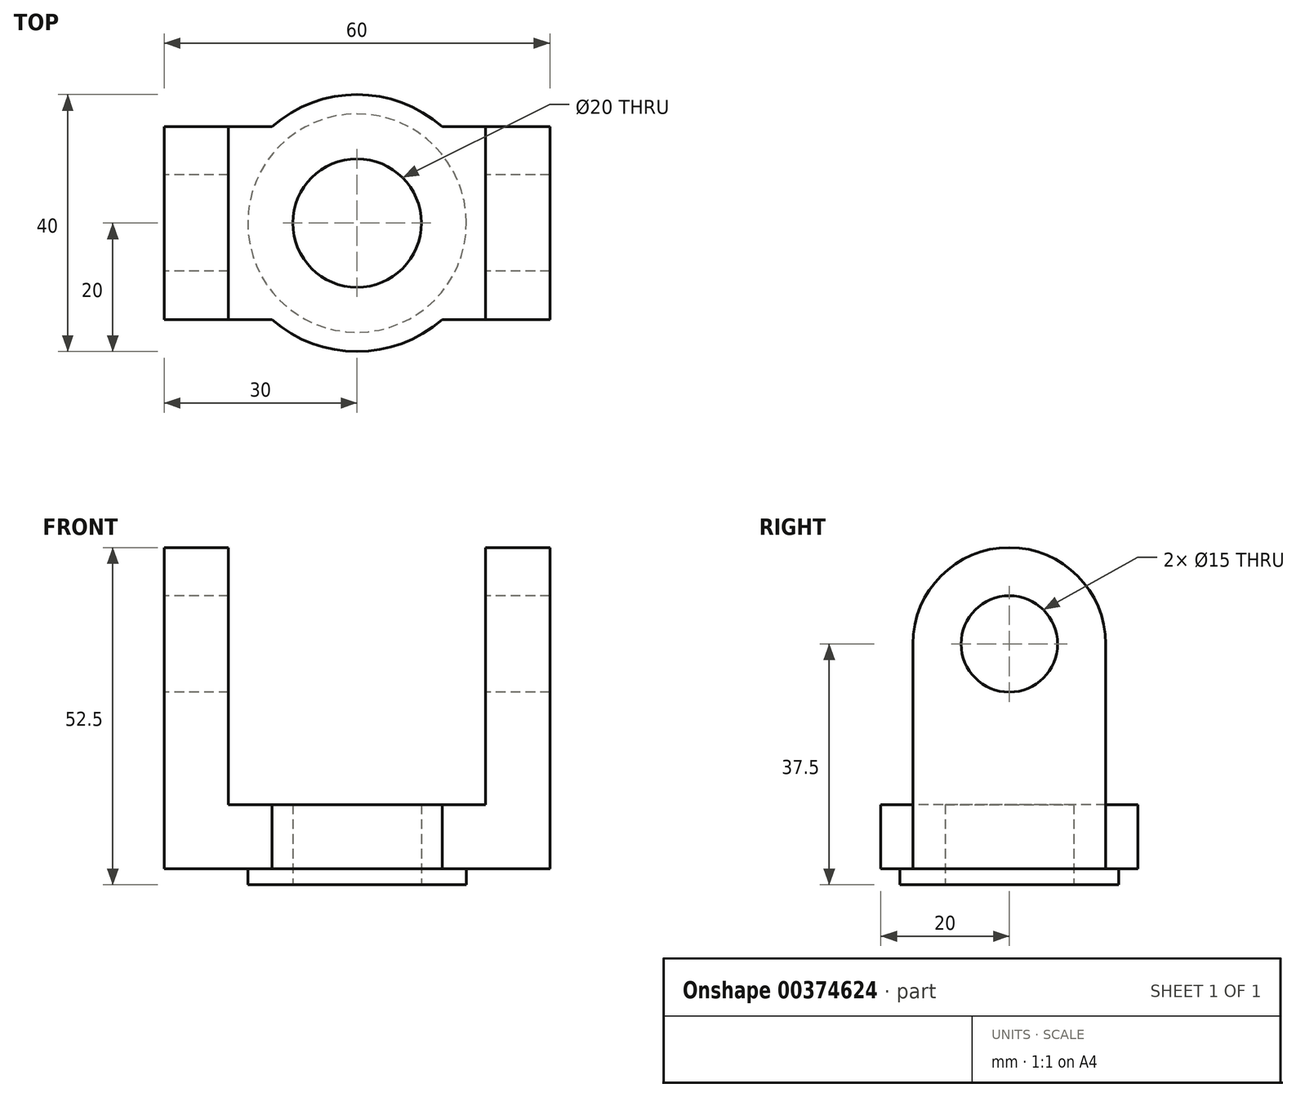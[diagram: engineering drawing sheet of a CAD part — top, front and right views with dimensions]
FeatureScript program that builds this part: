
annotation { "Feature Type Name" : "Feature", "Feature Type Description" : "" }
export const myFeature = defineFeature(function(context is Context, id is Id, definition is map)
    precondition{}
    {
        {
            var Q0;
            Q0=qCreatedBy(makeId("Right.planeOp"),FACE);
            var sketch = newSketch(context, id + "F0", { "sketchPlane" : qUnion([Q0])});
            skCircle(sketch, "E0", {"center": v(0, 35) * mm, "radius": 7.5 * mm});
            skLineSegment(sketch, "E1", {"start": v(-15, 0) * mm, "end": v(15, 0) * mm});
            skLineSegment(sketch, "E2", {"start": v(-15, 0) * mm, "end": v(-15, 35) * mm});
            skLineSegment(sketch, "E3", {"start": v(15, 0) * mm, "end": v(15, 35) * mm});
            skArc(sketch, "E4", {"start": v(15, 35) * mm, "mid": v(0, 50) * mm, "end": v(-15, 35) * mm});
            skSolve(sketch);
        }
        {
            var Q0;
            Q0 = qSketchRegion(id + "F0", true);
            extrude(context, id + "F1", {"entities" : qUnion([Q0]), "endBound" : BoundingType.SYMMETRIC, "depth" : 60 * mm});
        }
        {
            var Q0;
            Q0=qCreatedBy(makeId("Front.planeOp"),FACE);
            var sketch = newSketch(context, id + "F2", { "sketchPlane" : qUnion([Q0])});
            skLineSegment(sketch, "E5", {"start": v(-20, 50) * mm, "end": v(20, 50) * mm});
            skLineSegment(sketch, "E6", {"start": v(-20, 50) * mm, "end": v(-20, 10) * mm});
            skLineSegment(sketch, "E7", {"start": v(-20, 10) * mm, "end": v(20, 10) * mm});
            skLineSegment(sketch, "E8", {"start": v(20, 10) * mm, "end": v(20, 50) * mm});
            skSolve(sketch);
        }
        {
            var Q0;
            Q0 = qSketchRegion(id + "F2", true);
            extrude(context, id + "F3", {"entities" : qUnion([Q0]), "operationType" : NewBodyOperationType.REMOVE, "oppositeDirection" : true, "depth" : 25 * mm, "hasSecondDirection" : true, "secondDirectionOppositeDirection" : false, "secondDirectionDepth" : 25 * mm});
        }
        {
            var Q0;
            Q0=qCreatedBy(makeId("Top.planeOp"),FACE);
            var sketch = newSketch(context, id + "F4", { "sketchPlane" : qUnion([Q0])});
            skCircle(sketch, "E9", {"center": v(0, 0) * mm, "radius": 20 * mm});
            skSolve(sketch);
        }
        {
            var Q0;
            Q0 = qSketchRegion(id + "F4", true);
            extrude(context, id + "F5", {"entities" : qUnion([Q0]), "operationType" : NewBodyOperationType.ADD, "depth" : 10 * mm});
        }
        {
            var Q0;
            Q0=qCreatedBy(makeId("Top.planeOp"),FACE);
            var sketch = newSketch(context, id + "F6", { "sketchPlane" : qUnion([Q0])});
            skCircle(sketch, "E10", {"center": v(0, 0) * mm, "radius": 10 * mm});
            skSolve(sketch);
        }
        {
            var Q0;
            Q0 = qSketchRegion(id + "F6", true);
            extrude(context, id + "F7", {"entities" : qUnion([Q0]), "operationType" : NewBodyOperationType.REMOVE, "endBound" : BoundingType.THROUGH_ALL, "depth" : 25 * mm, "hasSecondDirection" : true, "secondDirectionOppositeDirection" : true, "secondDirectionDepth" : 25 * mm});
        }
        {
            var Q0;
            Q0=qCreatedBy(makeId("Top.planeOp"),FACE);
            var sketch = newSketch(context, id + "F8", { "sketchPlane" : qUnion([Q0])});
            skCircle(sketch, "E11", {"center": v(0, 0) * mm, "radius": 17 * mm});
            skSolve(sketch);
        }
        {
            var Q0;
            Q0 = qSketchRegion(id + "F8", true);
            extrude(context, id + "F9", {"entities" : qUnion([Q0]), "operationType" : NewBodyOperationType.ADD, "oppositeDirection" : true, "depth" : 2.5 * mm});
        }
        {
            var Q0;
            Q0=makeQuery(id+"F9.opExtrude","CAP_FACE",FACE,{"disambiguationData":[OSD([sQuery(id+"F8.wireOp",EDGE,"E11")])],"isStart":true});
            extrude(context, id + "F10", {"entities" : qUnion([Q0]), "operationType" : NewBodyOperationType.REMOVE, "oppositeDirection" : true, "depth" : 25 * mm});
        }
    });
